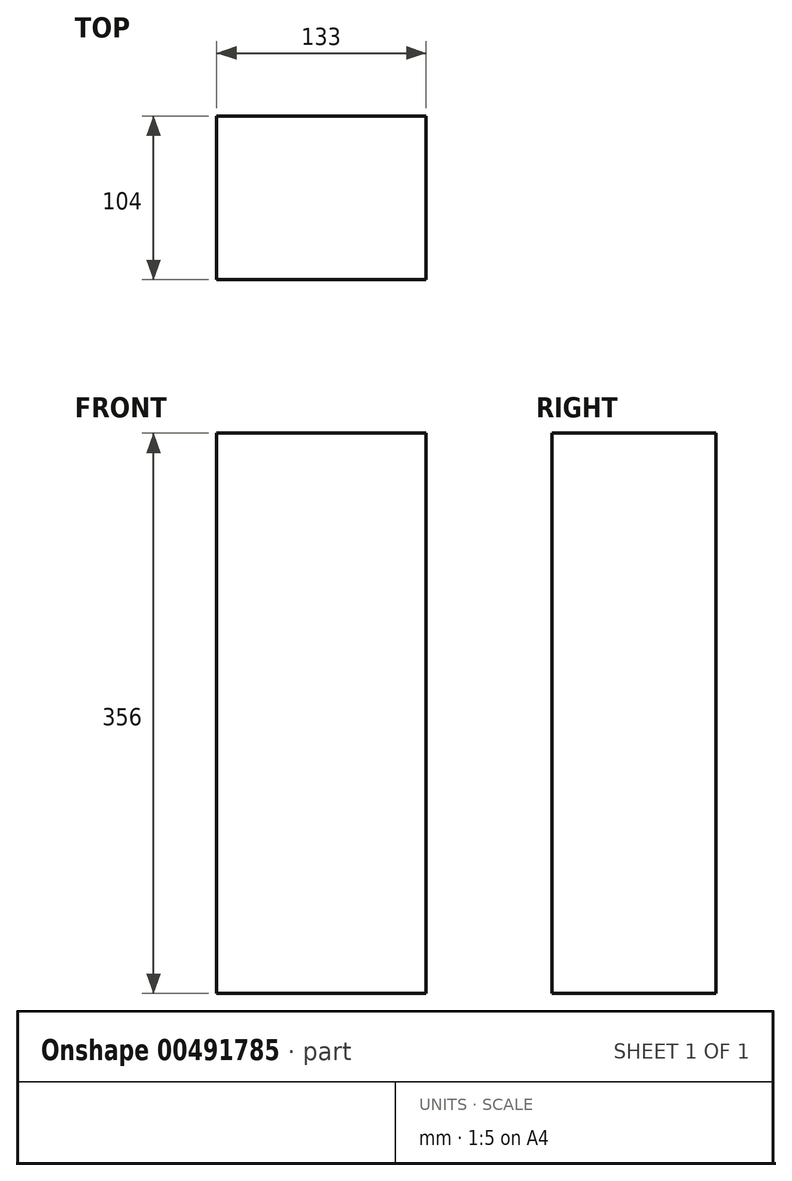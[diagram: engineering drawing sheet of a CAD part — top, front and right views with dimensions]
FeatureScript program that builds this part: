
annotation { "Feature Type Name" : "Feature", "Feature Type Description" : "" }
export const myFeature = defineFeature(function(context is Context, id is Id, definition is map)
    precondition{}
    {
        {
            var Q0;
            Q0=qCreatedBy(makeId("Front.planeOp"),FACE);
            var sketch = newSketch(context, id + "F0", { "sketchPlane" : qUnion([Q0])});
            skLineSegment(sketch, "E0.bottom", {"start": v(0, 0) * mm, "end": v(133, 0) * mm});
            skLineSegment(sketch, "E0.top", {"start": v(0, 356) * mm, "end": v(133, 356) * mm});
            skLineSegment(sketch, "E0.left", {"start": v(0, 0) * mm, "end": v(0, 356) * mm});
            skLineSegment(sketch, "E0.right", {"start": v(133, 0) * mm, "end": v(133, 356) * mm});
            skSolve(sketch);
        }
        {
            var Q0;
            Q0=makeQuery(id+"F0.imprint","IMPRINT",FACE,{"disambiguationData":[TD([[makeQuery(id+"F0.imprint","IMPRINT",EDGE,{"derivedFrom":sQuery(id+"F0.wireOp",EDGE,"E0.bottom")}),1.0]])]});
            extrude(context, id + "F1", {"entities" : qUnion([Q0]), "depth" : 104 * mm, "offsetDistance" : 25 * mm});
        }
    });
